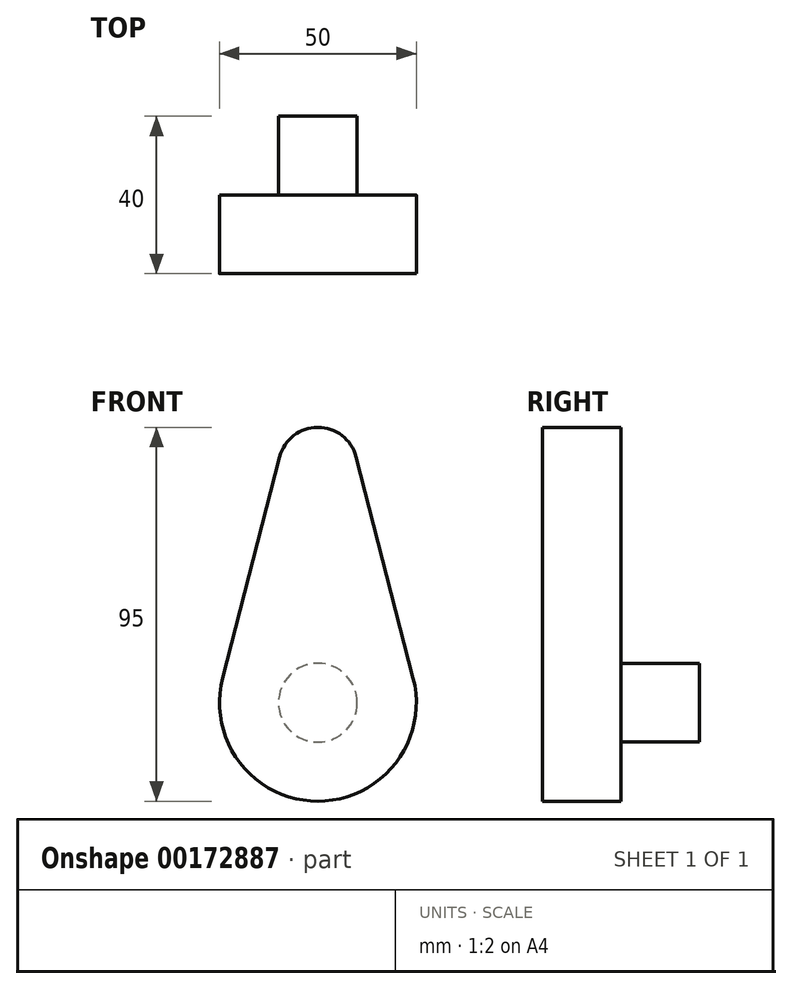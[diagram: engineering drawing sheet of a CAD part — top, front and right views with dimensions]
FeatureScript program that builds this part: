
annotation { "Feature Type Name" : "Feature", "Feature Type Description" : "" }
export const myFeature = defineFeature(function(context is Context, id is Id, definition is map)
    precondition{}
    {
        {
            var Q0;
            Q0=qCreatedBy(makeId("Front.planeOp"),FACE);
            var sketch = newSketch(context, id + "F0", { "sketchPlane" : qUnion([Q0])});
            skCircle(sketch, "E0", {"center": v(0, 0) * mm, "radius": 25 * mm});
            skCircle(sketch, "E1", {"center": v(0, 60) * mm, "radius": 10 * mm});
            skLineSegment(sketch, "E2", {"start": v(0, 60) * mm, "end": v(0, 0) * mm, "construction": true});
            skLineSegment(sketch, "E3", {"start": v(-9.68, 62.5) * mm, "end": v(-24.2, 6.25) * mm});
            skLineSegment(sketch, "E4.MirrorCS", {"start": v(9.68, 62.5) * mm, "end": v(24.2, 6.25) * mm});
            skSolve(sketch);
        }
        {
            var Q0;
            Q0 = qSketchRegion(id + "F0", true);
            extrude(context, id + "F1", {"entities" : qUnion([Q0]), "depth" : 20 * mm});
        }
        {
            var Q0;
            Q0=makeQuery(id+"F1.opExtrude","CAP_FACE",FACE,{"disambiguationData":[OSD([sQuery(id+"F0.wireOp",EDGE,"E0"),sQuery(id+"F0.wireOp",EDGE,"E1"),sQuery(id+"F0.wireOp",EDGE,"E3"),sQuery(id+"F0.wireOp",EDGE,"E4.MirrorCS")])],"isStart":true});
            var sketch = newSketch(context, id + "F2", { "sketchPlane" : qUnion([Q0])});
            skCircle(sketch, "E5", {"center": v(0, 0) * mm, "radius": 10 * mm});
            skSolve(sketch);
        }
        {
            var Q0;
            Q0 = qSketchRegion(id + "F2", true);
            extrude(context, id + "F3", {"entities" : qUnion([Q0]), "operationType" : NewBodyOperationType.ADD, "depth" : 20 * mm});
        }
    });
